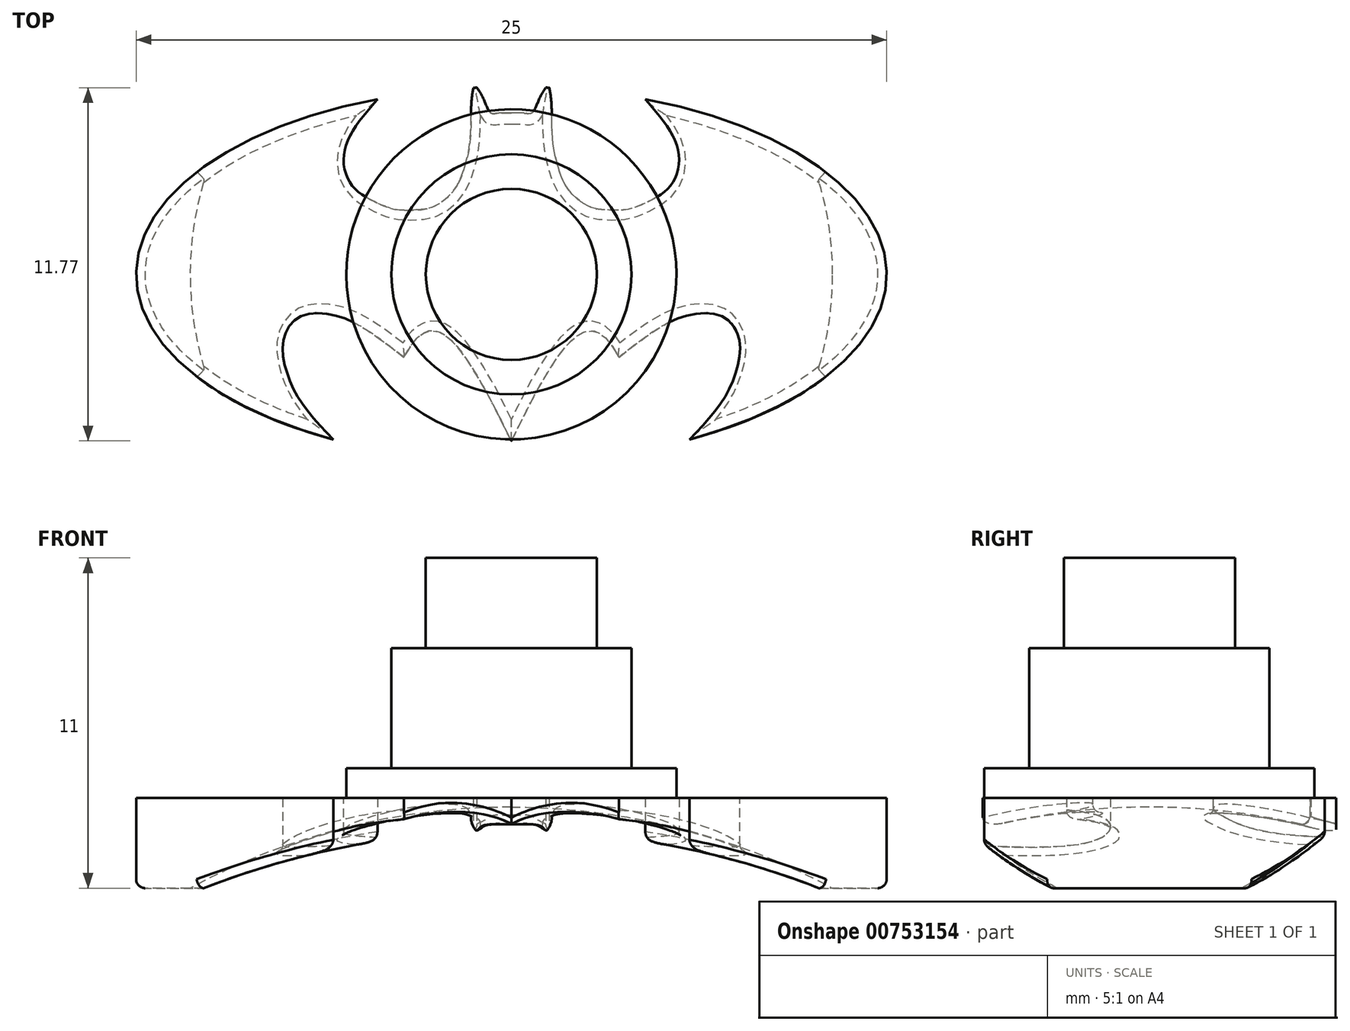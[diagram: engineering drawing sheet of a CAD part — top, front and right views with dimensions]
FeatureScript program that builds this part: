
annotation { "Feature Type Name" : "Feature", "Feature Type Description" : "" }
export const myFeature = defineFeature(function(context is Context, id is Id, definition is map)
    precondition{}
    {
        {
            var Q0;
            Q0=qCreatedBy(makeId("Top.planeOp"),FACE);
            var sketch = newSketch(context, id + "F0", { "sketchPlane" : qUnion([Q0])});
            skEllipticalArc(sketch, "E0", {});
            skFitSpline(sketch, "E1", {"points": [v(-4.46, 5.84) * mm, v(-5.29, 4.77) * mm, v(-5.59, 3.8) * mm, v(-5.32, 2.98) * mm, v(-4.7, 2.5) * mm, v(-3.86, 2.16) * mm, v(-3.2, 2.15) * mm, v(-2.63, 2.24) * mm, v(-1.92, 2.79) * mm, v(-1.58, 3.51) * mm, v(-1.38, 4.44) * mm, v(-1.34, 5.49) * mm, v(-1.26, 6.22) * mm], "startDerivative": vector(-6.9, -8.46) * mm, "endDerivative": vector(1.94, 8.78) * mm});
            skLineSegment(sketch, "E2", {"start": v(0, 0) * mm, "end": v(0, 8.48) * mm, "construction": true});
            skFitSpline(sketch, "E3", {"points": [v(-1.15, 6.22) * mm, v(-0.95, 5.9) * mm, v(-0.8, 5.56) * mm, v(-0.66, 5.36) * mm, v(-0.5, 5.36) * mm, v(-0.24, 5.38) * mm, v(0, 5.38) * mm], "startDerivative": vector(1, -1.46) * mm, "endDerivative": vector(2.36, 0) * mm});
            skLineSegment(sketch, "E4", {"start": v(0, 5.38) * mm, "end": v(0.24, 5.38) * mm, "construction": true});
            skFitSpline(sketch, "E5", {"points": [v(-5.93, -5.5) * mm, v(-6.91, -4.39) * mm, v(-7.47, -3.28) * mm, v(-7.59, -2.16) * mm, v(-7.04, -1.41) * mm, v(-5.77, -1.4) * mm, v(-4.58, -2.01) * mm, v(-3.58, -2.76) * mm], "startDerivative": vector(-6.75, 6.97) * mm, "endDerivative": vector(6.73, -5.3) * mm});
            skFitSpline(sketch, "E6", {"points": [v(0, -5.55) * mm, v(-0.77, -4.02) * mm, v(-1.45, -2.9) * mm, v(-2.1, -2.12) * mm, v(-2.72, -1.88) * mm, v(-3.26, -2.25) * mm, v(-3.58, -2.76) * mm], "startDerivative": vector(-5.35, 10.36) * mm, "endDerivative": vector(-3.6, -5.84) * mm});
            skFitSpline(sketch, "E7.MirrorCS", {"points": [v(4.46, 5.84) * mm, v(5.29, 4.77) * mm, v(5.59, 3.8) * mm, v(5.32, 2.98) * mm, v(4.7, 2.5) * mm, v(3.86, 2.16) * mm, v(3.2, 2.15) * mm, v(2.63, 2.24) * mm, v(1.92, 2.79) * mm, v(1.58, 3.51) * mm, v(1.38, 4.44) * mm, v(1.34, 5.49) * mm, v(1.26, 6.22) * mm], "startDerivative": vector(6.9, -8.46) * mm, "endDerivative": vector(-1.94, 8.78) * mm});
            skFitSpline(sketch, "E8.MirrorCS", {"points": [v(5.93, -5.5) * mm, v(6.91, -4.39) * mm, v(7.47, -3.28) * mm, v(7.59, -2.16) * mm, v(7.04, -1.41) * mm, v(5.77, -1.4) * mm, v(4.58, -2.01) * mm, v(3.58, -2.76) * mm], "startDerivative": vector(6.75, 6.97) * mm, "endDerivative": vector(-6.73, -5.3) * mm});
            skFitSpline(sketch, "E9.MirrorCS", {"points": [v(0, -5.55) * mm, v(0.77, -4.02) * mm, v(1.45, -2.9) * mm, v(2.1, -2.12) * mm, v(2.72, -1.88) * mm, v(3.26, -2.25) * mm, v(3.58, -2.76) * mm], "startDerivative": vector(5.35, 10.36) * mm, "endDerivative": vector(3.6, -5.84) * mm});
            skFitSpline(sketch, "E10.MirrorCS", {"points": [v(1.15, 6.22) * mm, v(0.95, 5.9) * mm, v(0.8, 5.56) * mm, v(0.66, 5.36) * mm, v(0.5, 5.36) * mm, v(0.24, 5.38) * mm, v(0, 5.38) * mm], "startDerivative": vector(-1, -1.46) * mm, "endDerivative": vector(-2.36, 0) * mm});
            skEllipticalArc(sketch, "E11.trimOffspring", {});
            skEllipticalArc(sketch, "E12.trimOffspring", {});
            skEllipticalArc(sketch, "E13.trimOffspring", {});
            const initialGuessF0  = {"E0": [0, 0, -1, 0, 0.0125, 0.00625, 5.077389266040888, 1.0763558123623582], "E11.trimOffspring": [0, 0, -1, 0, 0.0125, 0.00625, 4.804351116669659, 4.8136842039548124], "E12.trimOffspring": [0, 0, -1, 0, 0.0125, 0.00625, 4.611093756814567, 4.62042684409972], "E13.trimOffspring": [0, 0, -1, 0, 0.0125, 0.00625, 2.065236841227435, 4.34738869472849]};
            skSetInitialGuess(sketch, initialGuessF0);
            skSolve(sketch);
        }
        {
            var Q0;
            Q0=qSketchRegion(id+"F0",true);
            extrude(context, id + "F1", {"entities" : qUnion([Q0]), "depth" : 3 * mm, "offsetDistance" : 25 * mm});
        }
        {
            var Q0;
            Q0=qCreatedBy(makeId("Front.planeOp"),FACE);
            var sketch = newSketch(context, id + "F2", { "sketchPlane" : qUnion([Q0])});
            skLineSegment(sketch, "E14", {"start": v(0, 0) * mm, "end": v(0, -4.5) * mm, "construction": true});
            skSolve(sketch);
        }
        {
            var Q0;
            Q0=qCreatedBy(makeId("Front.planeOp"),FACE);
            var sketch = newSketch(context, id + "F3", { "sketchPlane" : qUnion([Q0])});
            skArc(sketch, "E15", {"start": v(0, 2.7) * mm, "mid": v(-22.55, -19.85) * mm, "end": v(0, -42.4) * mm});
            skLineSegment(sketch, "E16", {"start": v(0, 2.7) * mm, "end": v(0, -42.4) * mm});
            skPoint(sketch, "E17", {"position": v(-10.7, 0) * mm});
            skSolve(sketch);
        }
        {
            var Q0;
            Q0=qSketchRegion(id+"F3",true);
            var Q1;
            Q1=sQuery(id+"F3.wireOp",EDGE,"E16");
            revolve(context, id + "F4", {"operationType" : NewBodyOperationType.REMOVE, "surfaceOperationType" : NewSurfaceOperationType.NEW, "entities" : qUnion([Q0]), "axis" : qUnion([Q1]), "revolveType" : RevolveType.FULL, "oppositeDirection" : true});
        }
        {
            var Q0;
            Q0=makeQuery(id+"F1.opExtrude","CAP_FACE",FACE,{"disambiguationData":[OSD([sQuery(id+"F0.wireOp",EDGE,"E0"),sQuery(id+"F0.wireOp",EDGE,"E1"),sQuery(id+"F0.wireOp",EDGE,"E3"),sQuery(id+"F0.wireOp",EDGE,"E5"),sQuery(id+"F0.wireOp",EDGE,"E6"),sQuery(id+"F0.wireOp",EDGE,"E7.MirrorCS"),sQuery(id+"F0.wireOp",EDGE,"E8.MirrorCS"),sQuery(id+"F0.wireOp",EDGE,"E9.MirrorCS"),sQuery(id+"F0.wireOp",EDGE,"E10.MirrorCS"),sQuery(id+"F0.wireOp",EDGE,"E11.trimOffspring"),sQuery(id+"F0.wireOp",EDGE,"E12.trimOffspring"),sQuery(id+"F0.wireOp",EDGE,"E13.trimOffspring")])],"isStart":false});
            var sketch = newSketch(context, id + "F5", { "sketchPlane" : qUnion([Q0])});
            skCircle(sketch, "E18", {"center": v(0, 0) * mm, "radius": 5.5 * mm});
            skSolve(sketch);
        }
        {
            var Q0;
            Q0=qSketchRegion(id+"F5",true);
            extrude(context, id + "F6", {"entities" : qUnion([Q0]), "operationType" : NewBodyOperationType.ADD, "depth" : 1 * mm, "offsetDistance" : 25 * mm});
        }
        {
            var Q0;
            Q0=makeQuery(id+"F6.opExtrude","CAP_FACE",FACE,{"disambiguationData":[OSD([sQuery(id+"F5.wireOp",EDGE,"E18")])],"isStart":false});
            var sketch = newSketch(context, id + "F7", { "sketchPlane" : qUnion([Q0])});
            skCircle(sketch, "E19", {"center": v(0, 0) * mm, "radius": 4 * mm});
            skSolve(sketch);
        }
        {
            var Q0;
            Q0=qSketchRegion(id+"F7",true);
            extrude(context, id + "F8", {"entities" : qUnion([Q0]), "operationType" : NewBodyOperationType.ADD, "depth" : 4 * mm, "offsetDistance" : 25 * mm});
        }
        {
            var Q0;
            Q0=makeQuery(id+"F8.opExtrude","CAP_FACE",FACE,{"disambiguationData":[OSD([sQuery(id+"F7.wireOp",EDGE,"E19")])],"isStart":false});
            var sketch = newSketch(context, id + "F9", { "sketchPlane" : qUnion([Q0])});
            skCircle(sketch, "E20", {"center": v(0, 0) * mm, "radius": 2.85 * mm});
            skSolve(sketch);
        }
        {
            var Q0;
            Q0=qSketchRegion(id+"F9",true);
            extrude(context, id + "F10", {"entities" : qUnion([Q0]), "operationType" : NewBodyOperationType.ADD, "depth" : 3 * mm, "offsetDistance" : 25 * mm});
        }
        {
            var Q0;
            Q0=makeQuery(id+"F1.opExtrude","CAP_EDGE",EDGE,{"disambiguationData":[OSD([sQuery(id+"F0.wireOp",EDGE,"E13.trimOffspring")])],"isStart":true});
            var Q1;
            Q1=makeQuery(id+"F4.boolean.opBoolean","INTERSECT",EDGE,{"disambiguationData":[OD(0.0)],"derivedFrom":[makeQuery(id+"F1.opExtrude","SWEPT_FACE",FACE,{"disambiguationData":[OSD([sQuery(id+"F0.wireOp",EDGE,"E13.trimOffspring")])]}),makeQuery(id+"F4.opRevolve","SWEPT_FACE",FACE,{"disambiguationData":[OSD([sQuery(id+"F3.wireOp",EDGE,"E15")])]})]});
            var Q2;
            Q2=makeQuery(id+"F4.boolean.opBoolean","INTERSECT",EDGE,{"disambiguationData":[OD(1.0)],"derivedFrom":[makeQuery(id+"F1.opExtrude","SWEPT_FACE",FACE,{"disambiguationData":[OSD([sQuery(id+"F0.wireOp",EDGE,"E13.trimOffspring")])]}),makeQuery(id+"F4.opRevolve","SWEPT_FACE",FACE,{"disambiguationData":[OSD([sQuery(id+"F3.wireOp",EDGE,"E15")])]})]});
            var Q3;
            Q3=makeQuery(id+"F4.boolean.opBoolean","INTERSECT",EDGE,{"disambiguationData":[OD(1.0)],"derivedFrom":[makeQuery(id+"F1.opExtrude","SWEPT_FACE",FACE,{"disambiguationData":[OSD([sQuery(id+"F0.wireOp",EDGE,"E0")])]}),makeQuery(id+"F4.opRevolve","SWEPT_FACE",FACE,{"disambiguationData":[OSD([sQuery(id+"F3.wireOp",EDGE,"E15")])]})]});
            var Q4;
            Q4=makeQuery(id+"F1.opExtrude","CAP_EDGE",EDGE,{"disambiguationData":[OSD([sQuery(id+"F0.wireOp",EDGE,"E0")])],"isStart":true});
            var Q5;
            Q5=makeQuery(id+"F4.boolean.opBoolean","INTERSECT",EDGE,{"disambiguationData":[OD(0.0)],"derivedFrom":[makeQuery(id+"F1.opExtrude","SWEPT_FACE",FACE,{"disambiguationData":[OSD([sQuery(id+"F0.wireOp",EDGE,"E0")])]}),makeQuery(id+"F4.opRevolve","SWEPT_FACE",FACE,{"disambiguationData":[OSD([sQuery(id+"F3.wireOp",EDGE,"E15")])]})]});
            var Q6;
            Q6=makeQuery(id+"F4.boolean.opBoolean","INTERSECT",EDGE,{"derivedFrom":[makeQuery(id+"F1.opExtrude","SWEPT_FACE",FACE,{"disambiguationData":[OSD([sQuery(id+"F0.wireOp",EDGE,"E5")])]}),makeQuery(id+"F4.opRevolve","SWEPT_FACE",FACE,{"disambiguationData":[OSD([sQuery(id+"F3.wireOp",EDGE,"E15")])]})]});
            var Q7;
            Q7=makeQuery(id+"F4.boolean.opBoolean","INTERSECT",EDGE,{"derivedFrom":[makeQuery(id+"F1.opExtrude","SWEPT_FACE",FACE,{"disambiguationData":[OSD([sQuery(id+"F0.wireOp",EDGE,"E6")])]}),makeQuery(id+"F4.opRevolve","SWEPT_FACE",FACE,{"disambiguationData":[OSD([sQuery(id+"F3.wireOp",EDGE,"E15")])]})]});
            var Q8;
            Q8=makeQuery(id+"F4.boolean.opBoolean","INTERSECT",EDGE,{"derivedFrom":[makeQuery(id+"F1.opExtrude","SWEPT_FACE",FACE,{"disambiguationData":[OSD([sQuery(id+"F0.wireOp",EDGE,"E9.MirrorCS")])]}),makeQuery(id+"F4.opRevolve","SWEPT_FACE",FACE,{"disambiguationData":[OSD([sQuery(id+"F3.wireOp",EDGE,"E15")])]})]});
            var Q9;
            Q9=makeQuery(id+"F4.boolean.opBoolean","INTERSECT",EDGE,{"derivedFrom":[makeQuery(id+"F1.opExtrude","SWEPT_FACE",FACE,{"disambiguationData":[OSD([sQuery(id+"F0.wireOp",EDGE,"E8.MirrorCS")])]}),makeQuery(id+"F4.opRevolve","SWEPT_FACE",FACE,{"disambiguationData":[OSD([sQuery(id+"F3.wireOp",EDGE,"E15")])]})]});
            var Q10;
            Q10=makeQuery(id+"F4.boolean.opBoolean","INTERSECT",EDGE,{"derivedFrom":[makeQuery(id+"F1.opExtrude","SWEPT_FACE",FACE,{"disambiguationData":[OSD([sQuery(id+"F0.wireOp",EDGE,"E7.MirrorCS")])]}),makeQuery(id+"F4.opRevolve","SWEPT_FACE",FACE,{"disambiguationData":[OSD([sQuery(id+"F3.wireOp",EDGE,"E15")])]})]});
            var Q11;
            Q11=makeQuery(id+"F4.boolean.opBoolean","INTERSECT",EDGE,{"derivedFrom":[makeQuery(id+"F1.opExtrude","SWEPT_FACE",FACE,{"disambiguationData":[OSD([sQuery(id+"F0.wireOp",EDGE,"E1")])]}),makeQuery(id+"F4.opRevolve","SWEPT_FACE",FACE,{"disambiguationData":[OSD([sQuery(id+"F3.wireOp",EDGE,"E15")])]})]});
            var Q12;
            Q12=makeQuery(id+"F4.boolean.opBoolean","INTERSECT",EDGE,{"derivedFrom":[makeQuery(id+"F1.opExtrude","SWEPT_FACE",FACE,{"disambiguationData":[OSD([sQuery(id+"F0.wireOp",EDGE,"E10.MirrorCS")])]}),makeQuery(id+"F4.opRevolve","SWEPT_FACE",FACE,{"disambiguationData":[OSD([sQuery(id+"F3.wireOp",EDGE,"E15")])]})]});
            fillet(context, id + "F11", {"entities" : qUnion([Q0, Q1, Q2, Q3, Q4, Q5, Q6, Q7, Q8, Q9, Q10, Q11, Q12]), "radius" : 0.3 * mm, "tangentPropagation" : true, "allowEdgeOverflow" : false});
        }
    });
